# Revit family: Wall_Panel-Teknion-CWPL-Above_Low_Credenza-R2021
name_source: partatom
category: Furniture
units: mm (PartAtom-declared; Revit-internal decimal feet)

## family parameters
Always vertical = Yes
Cut with Voids When Loaded = No
OmniClass Number = 23.40.20.00
OmniClass Title = General Furniture and Specialties
Room Calculation Point = No
Shared = Yes
Work Plane-Based = No

## types (5) — shared parameters
Assembly Code = E2020200
Manufacturer = Teknion
Manufacturer Fax = 416.661.4586
Part Number = CWPL
Product Documentation Link = https://www.teknion.com
Product Line = Chronicle
Product Page URL = https://www.teknion.com
Series = Chronicle
Sustainability Data = https://www.teknion.com
URL = www.teknion.com
Unit Weight URL = http://www.teknion.com
Warranty = http://www.teknion.com
zero-valued in all types: Default Elevation

## per-type parameters (varying)
| type | Description | Height | Model |
| (1L) 1 High, 19.5" | Wall Panel, Above Low Credenza, 1 High-19.5",Full Height | 19.5 " | CWPL1LF__ |
| (2L) 2 High, 33.25" | Wall Panel, Above Low Credenza, 2 High-33.25",Full Height | 33.25 " | CWPL2LF__ |
| (3L) 3 High, 48" | Wall Panel, Above Low Credenza, 3 High-48",Full Height | 48 " | CWPL3LF__ |
| (4L) 4 High, 61.75" | Wall Panel, Above Low Credenza, 4 High-61.75",Full Height | 61.75 " | CWPL4LF__ |
| (3L) 3 High, Reduced Height by 1" | Wall Panel, Above Low Credenza,3 Hight-47",Reduced Height by 1" | 47 " | CWPL3LR__ |

## geometry (parser evidence)
native form markers: Sweep x4
no freeform markers — native parametric forms only
